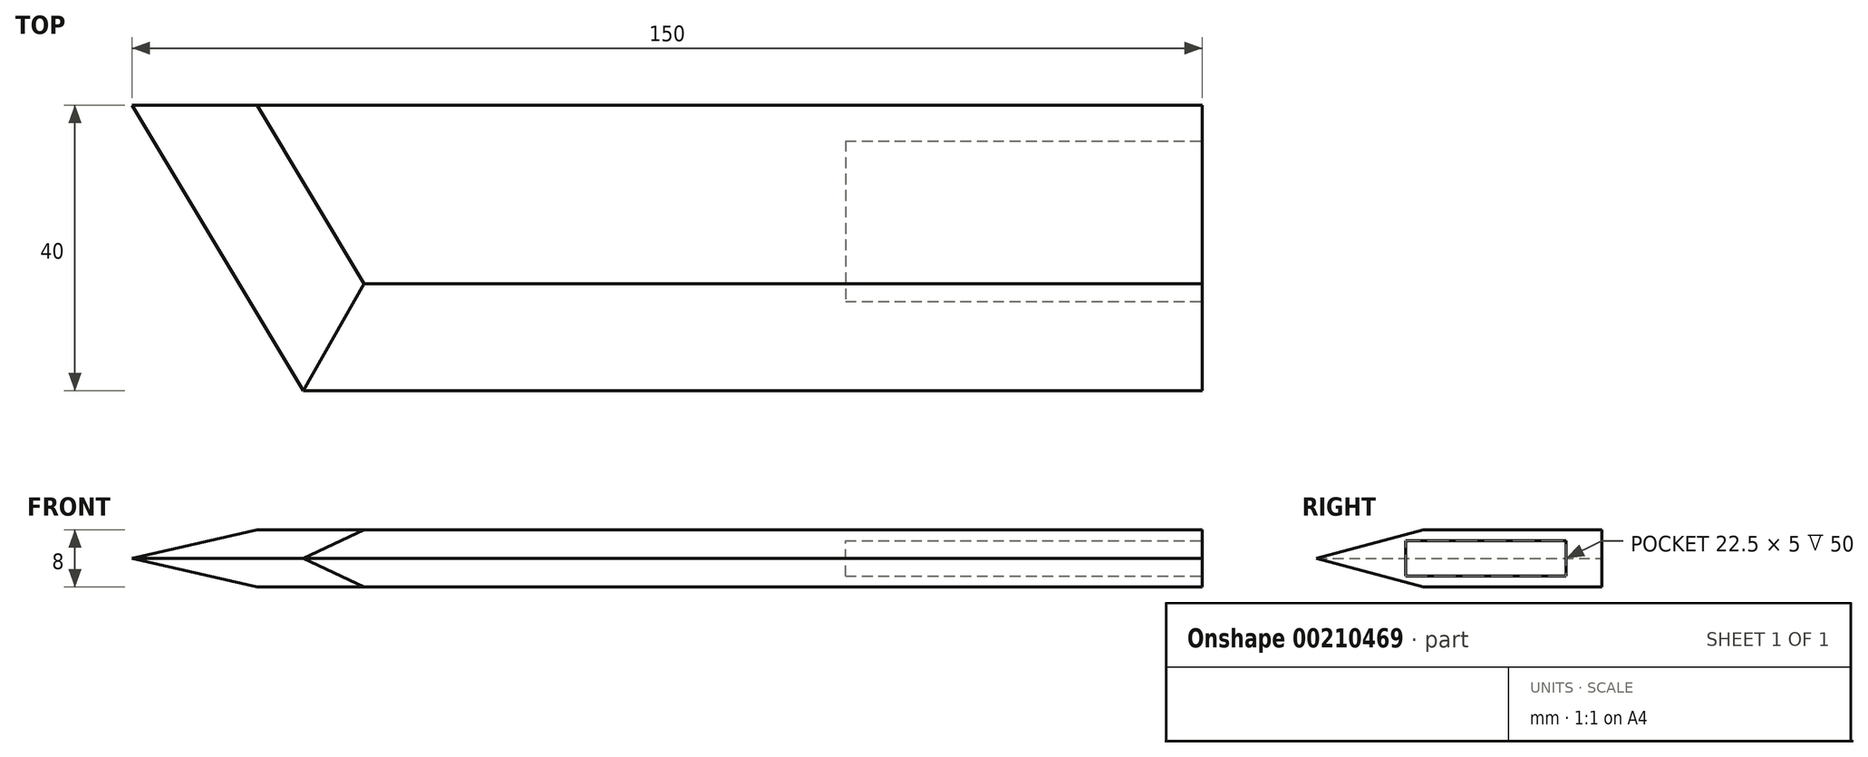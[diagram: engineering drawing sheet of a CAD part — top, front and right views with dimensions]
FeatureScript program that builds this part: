
annotation { "Feature Type Name" : "Feature", "Feature Type Description" : "" }
export const myFeature = defineFeature(function(context is Context, id is Id, definition is map)
    precondition{}
    {
        {
            var Q0;
            Q0=qCreatedBy(makeId("Top.planeOp"),FACE);
            var sketch = newSketch(context, id + "F0", { "sketchPlane" : qUnion([Q0])});
            skLineSegment(sketch, "E0", {"start": v(0, 0) * mm, "end": v(0, 40) * mm});
            skLineSegment(sketch, "E1", {"start": v(0, 40) * mm, "end": v(-150, 40) * mm});
            skLineSegment(sketch, "E2", {"start": v(0, 0) * mm, "end": v(-126, 0) * mm});
            skLineSegment(sketch, "E3", {"start": v(-126, 0) * mm, "end": v(-150, 40) * mm});
            skSolve(sketch);
        }
        {
            var Q0;
            Q0 = qSketchRegion(id + "F0", true);
            extrude(context, id + "F1", {"entities" : qUnion([Q0]), "depth" : 8 * mm});
        }
        {
            var Q0;
            Q0=makeQuery(id+"F1.opExtrude","CAP_EDGE",EDGE,{"disambiguationData":[OSD([sQuery(id+"F0.wireOp",EDGE,"E2")])],"isStart":false});
            var Q1;
            Q1=makeQuery(id+"F1.opExtrude","CAP_EDGE",EDGE,{"disambiguationData":[OSD([sQuery(id+"F0.wireOp",EDGE,"E3")])],"isStart":false});
            var Q2;
            Q2=makeQuery(id+"F1.opExtrude","CAP_EDGE",EDGE,{"disambiguationData":[OSD([sQuery(id+"F0.wireOp",EDGE,"E2")])],"isStart":true});
            chamfer(context, id + "F2", {"entities" : qUnion([Q0, Q1, Q2]), "chamferType" : ChamferType.TWO_OFFSETS, "width1" : 4 * mm, "oppositeDirection" : false, "width2" : 15 * mm, "tangentPropagation" : true});
        }
        {
            var Q0;
            Q0=makeQuery(id+"F1.opExtrude","CAP_EDGE",EDGE,{"disambiguationData":[OSD([sQuery(id+"F0.wireOp",EDGE,"E3")])],"isStart":true});
            chamfer(context, id + "F3", {"entities" : qUnion([Q0]), "chamferType" : ChamferType.TWO_OFFSETS, "width1" : 15 * mm, "oppositeDirection" : false, "width2" : 4 * mm, "tangentPropagation" : true});
        }
        {
            var Q0;
            Q0=makeQuery(id+"F1.opExtrude","SWEPT_FACE",FACE,{"disambiguationData":[OSD([sQuery(id+"F0.wireOp",EDGE,"E0")])]});
            var sketch = newSketch(context, id + "F4", { "sketchPlane" : qUnion([Q0])});
            skLineSegment(sketch, "E4", {"start": v(0, 4) * mm, "end": v(12.5, 4) * mm});
            skLineSegment(sketch, "E5", {"start": v(12.5, 4) * mm, "end": v(12.5, 6.5) * mm});
            skLineSegment(sketch, "E6", {"start": v(12.5, 6.5) * mm, "end": v(35, 6.5) * mm});
            skLineSegment(sketch, "E7", {"start": v(35, 6.5) * mm, "end": v(35, 1.5) * mm});
            skLineSegment(sketch, "E8", {"start": v(35, 1.5) * mm, "end": v(12.5, 1.5) * mm});
            skLineSegment(sketch, "E9", {"start": v(12.5, 1.5) * mm, "end": v(12.5, 4) * mm});
            skSolve(sketch);
        }
        {
            var Q0;
            Q0 = qSketchRegion(id + "F4", true);
            extrude(context, id + "F5", {"entities" : qUnion([Q0]), "operationType" : NewBodyOperationType.REMOVE, "oppositeDirection" : true, "depth" : 50 * mm});
        }
    });
